# Revit family: WashbasinUnit-78cm-With2Drawer-Vitra-SentoSeries-60824+60830+60836
name_source: partatom
category: Furniture Systems
revit_build: Autodesk Revit 2017 (Build: 20160225_1515(x64)
units: mm (PartAtom-declared; Revit-internal decimal feet)

## family parameters
Cut with Voids When Loaded = No
Host = Face
OmniClass Number = 23.40.00.00
OmniClass Title = Equipment and Furnishings
Part Type = Normal
Room Calculation Point = No
Round Connector Dimension = Use Diameter
Shared = Yes

## types (3) — shared parameters
BIMobject category = Bathroom compound units
Brand = VitrA
Default Elevation = 850 mm  [stored 2.78871 ft]
Description = Sento Washbasin Unit - 78cm - with 2 drawer
Design country = Turkey
IFC Classification = Furniture
Lighting Type = Led Lighting
Main Material = Wood
Manufacturer = VitrA
Manufacturer name = VitrA
Masterformat 2014 Code = 13 42 13
Masterformat 2014 Description = Bathroom Unit Modules
Mounting type = Wall-Hung
NBS Referans Code = 35-75-08
NBS Referans Description = Bathroom Cabinets
Nominal Depth (mm) = 445 mm  [stored 1.45997 ft]
Nominal Height (mm) = 615 mm  [stored 2.01772 ft]
Nominal Width (mm) = 700 mm  [stored 2.29659 ft]
OmniClass Code = 23-31 25 13
OmniClass Description = Bathroom Cabinets
Product certification = https://www.vitraglobal.com
Product data url = https://www.vitra-bad.de
Product family = Sento
Product group = Washbasin Unit
Secondary Material = Natural Oak
Technical description = https://cdn.vitra.com.tr
UNSPSC Code = 301815
UNSPSC Description = Bathroom Cabinets
URL = https://vitraglobal.com
Uniclass 1.4 Code = L8241
Uniclass 1.4 Description = Bathroom Cabinets
Uniclass 2.0 Code = PR-35-75-08
Uniclass 2.0 Description = Bathroom Cabinets
Uniclass 2015 Code = Pr_40_20_93
Uniclass 2015 Name = Wash basins, sinks and troughs
Uniformat II Code = E20
Uniformat II Description = FURNISHINGS
Voltage(V) = 220
Warranty Period (Year) = 2
Weight Net (kg) = 62.1
Youtube = https://www.youtube.com

## per-type parameters (varying)
| type | Article No. (default) | Color | Model | Primary Material | Product SKU |
| Sento Washbasin Unit, 78cm, with 2 drawer, Matte Cream-60830 | 60830 | Matte Cream | 60830 | Cream matte | 60830 |
| Sento Washbasin Unit, 78cm, with 2 drawer, Matte Anthracite-60836 | 60836 | Matt Anthracite | 60836 | Anthracite matte | 60836 |
| Sento Washbasin Unit, 78cm, with 2 drawer, Matte White-60824 | 60824 | Matte White | 60824 | MattWhite | 60824 |

note: [stored X ft] marks values corroborated as IEEE doubles in the binary element streams (Revit-internal decimal feet)

## geometry (parser evidence)
native form markers: Sweep x4
no freeform markers — native parametric forms only
